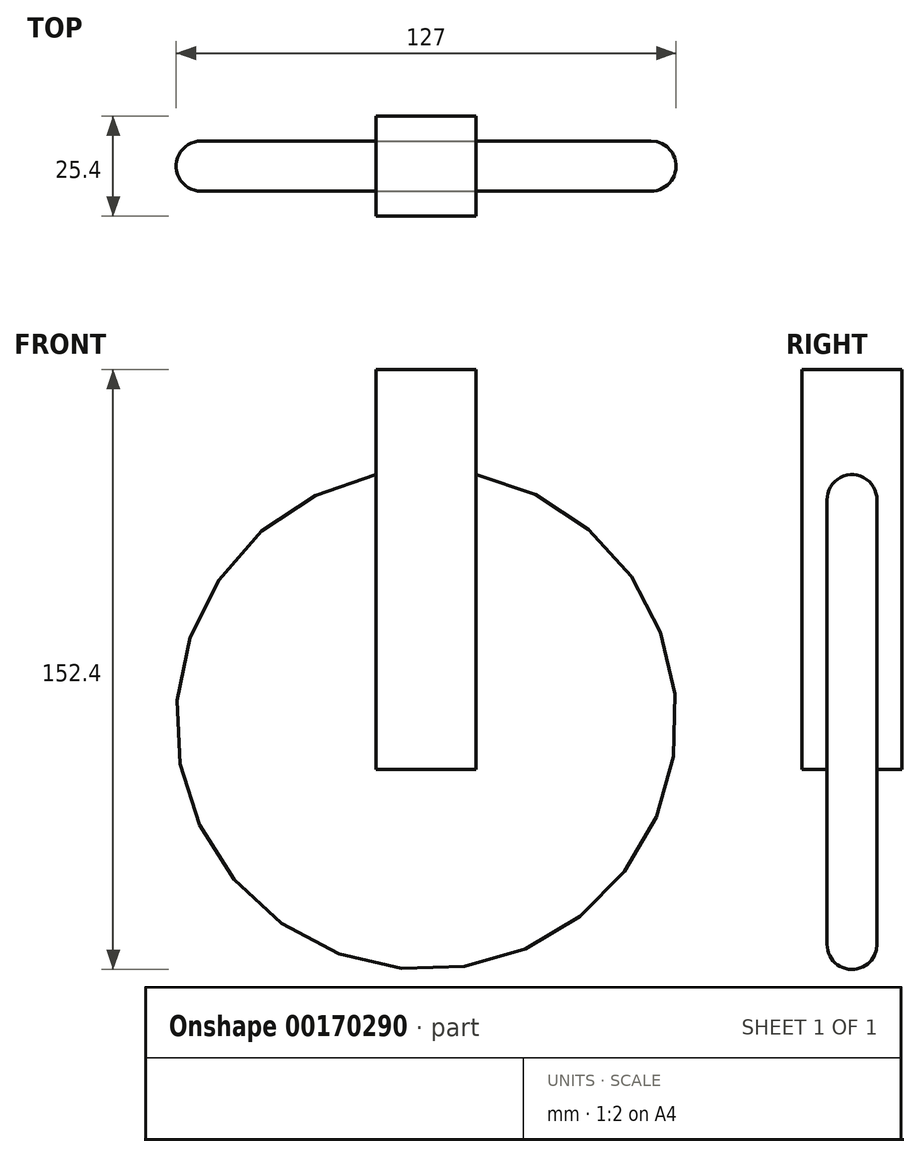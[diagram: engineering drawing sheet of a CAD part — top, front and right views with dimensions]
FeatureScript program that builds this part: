
annotation { "Feature Type Name" : "Feature", "Feature Type Description" : "" }
export const myFeature = defineFeature(function(context is Context, id is Id, definition is map)
    precondition{}
    {
        {
            var Q0;
            Q0=qCreatedBy(makeId("Front.planeOp"),FACE);
            var sketch = newSketch(context, id + "F0", { "sketchPlane" : qUnion([Q0])});
            skCircle(sketch, "E0", {"center": v(0, 0) * mm, "radius": 63.5 * mm});
            skCircle(sketch, "E1", {"center": v(0, 0) * mm, "radius": 6.35 * mm});
            skSolve(sketch);
        }
        {
            var Q0;
            Q0 = qSketchRegion(id + "F0", true);
            extrude(context, id + "F1", {"entities" : qUnion([Q0]), "endBound" : BoundingType.SYMMETRIC, "depth" : 12.7 * mm});
        }
        {
            var Q0;
            Q0=makeQuery(id+"F1.opExtrude","CAP_EDGE",EDGE,{"disambiguationData":[OSD([sQuery(id+"F0.wireOp",EDGE,"E0")])],"isStart":false});
            var Q1;
            Q1=makeQuery(id+"F1.opExtrude","CAP_EDGE",EDGE,{"disambiguationData":[OSD([sQuery(id+"F0.wireOp",EDGE,"E0")])],"isStart":true});
            fillet(context, id + "F2", {"entities" : qUnion([Q0, Q1]), "radius" : 6.35 * mm, "tangentPropagation" : true, "allowEdgeOverflow" : false});
        }
        {
            var Q0;
            Q0=qCreatedBy(makeId("Right.planeOp"),FACE);
            var sketch = newSketch(context, id + "F3", { "sketchPlane" : qUnion([Q0])});
            skLineSegment(sketch, "E2", {"start": v(0, 0) * mm, "end": v(0, -12.7) * mm});
            skLineSegment(sketch, "E3", {"start": v(0, -12.7) * mm, "end": v(-12.7, -12.7) * mm});
            skLineSegment(sketch, "E4.bottom", {"start": v(-12.7, -12.7) * mm, "end": v(12.7, -12.7) * mm});
            skLineSegment(sketch, "E4.top", {"start": v(-12.7, 88.9) * mm, "end": v(12.7, 88.9) * mm});
            skLineSegment(sketch, "E4.left", {"start": v(-12.7, -12.7) * mm, "end": v(-12.7, 88.9) * mm});
            skLineSegment(sketch, "E4.right", {"start": v(12.7, -12.7) * mm, "end": v(12.7, 88.9) * mm});
            skSolve(sketch);
        }
        {
            var Q0;
            Q0 = qSketchRegion(id + "F3", true);
            extrude(context, id + "F4", {"entities" : qUnion([Q0]), "operationType" : NewBodyOperationType.ADD, "endBound" : BoundingType.SYMMETRIC, "depth" : 25.4 * mm});
        }
    });
